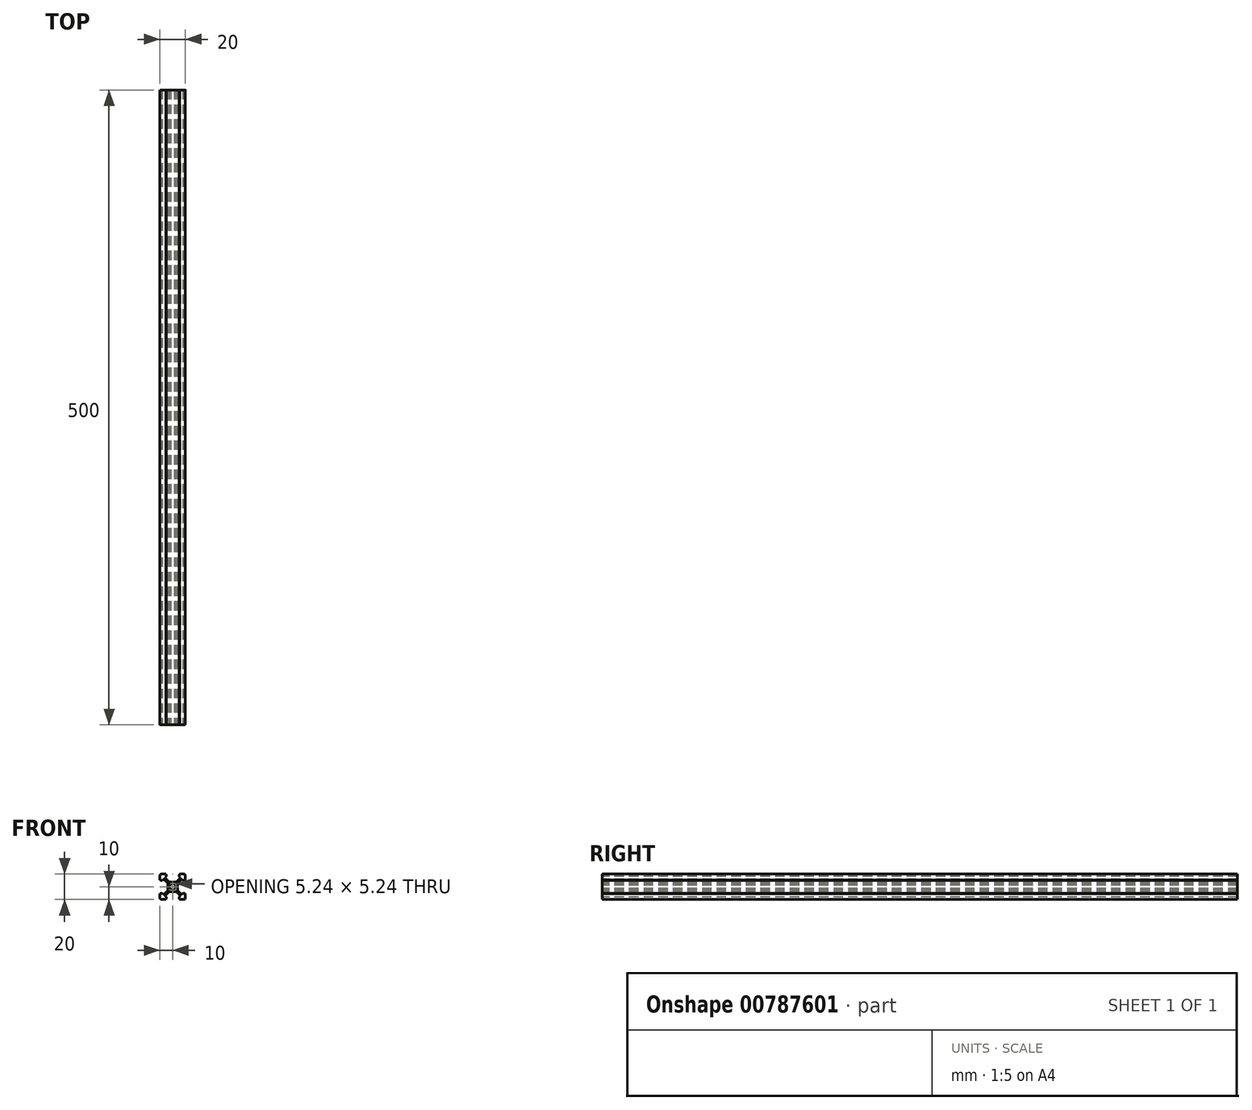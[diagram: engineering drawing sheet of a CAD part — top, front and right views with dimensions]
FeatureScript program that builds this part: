
annotation { "Feature Type Name" : "Feature", "Feature Type Description" : "" }
export const myFeature = defineFeature(function(context is Context, id is Id, definition is map)
    precondition{}
    {
        {
            var Q0;
            Q0=qCreatedBy(makeId("Front.planeOp"),FACE);
            var sketch = newSketch(context, id + "F0", { "sketchPlane" : qUnion([Q0])});
            skLineSegment(sketch, "E0", {"start": v(-10, 5.5) * mm, "end": v(-10, 9) * mm});
            skLineSegment(sketch, "E1", {"start": v(-9, 10) * mm, "end": v(-5.5, 10) * mm});
            skPoint(sketch, "E2.visualSharp", {"position": v(-10, 10) * mm});
            skArc(sketch, "E2.filletArc", {"start": v(-9, 10) * mm, "mid": v(-9.7, 9.7) * mm, "end": v(-10, 9) * mm});
            skPoint(sketch, "E3.end.orphan", {"position": v(0, 8) * mm});
            skPoint(sketch, "E4.start.orphan", {"position": v(-8, 0) * mm});
            skLineSegment(sketch, "E5", {"start": v(-10, 5.5) * mm, "end": v(-9.5, 5.5) * mm});
            skLineSegment(sketch, "E6", {"start": v(-9.5, 5.5) * mm, "end": v(-9.5, 5) * mm});
            skLineSegment(sketch, "E7", {"start": v(-9.5, 5) * mm, "end": v(-8.1, 5) * mm});
            skLineSegment(sketch, "E8", {"start": v(-8.1, 4.97) * mm, "end": v(-8.1, 5) * mm});
            skPoint(sketch, "E9.end.orphan", {"position": v(-3.5, 0) * mm});
            skLineSegment(sketch, "E10.bottom", {"start": v(2.84, 3.9) * mm, "end": v(-2.84, 3.9) * mm});
            skLineSegment(sketch, "E10.top", {"start": v(2.84, -3.9) * mm, "end": v(-2.84, -3.9) * mm});
            skLineSegment(sketch, "E10.left", {"start": v(3.9, 2.84) * mm, "end": v(3.9, -2.84) * mm});
            skLineSegment(sketch, "E10.right", {"start": v(-3.9, 2.84) * mm, "end": v(-3.9, -2.84) * mm});
            skPoint(sketch, "E10.middle", {"position": v(0, 0) * mm});
            skPoint(sketch, "E11.orphan", {"position": v(0, 9) * mm});
            skLineSegment(sketch, "E12.MirrorCS", {"start": v(-5.5, 10) * mm, "end": v(-9, 10) * mm});
            skLineSegment(sketch, "E13.MirrorCS", {"start": v(-5.5, 10) * mm, "end": v(-5.5, 9.5) * mm});
            skLineSegment(sketch, "E14.MirrorCS", {"start": v(-5.5, 9.5) * mm, "end": v(-5, 9.5) * mm});
            skLineSegment(sketch, "E15.MirrorCS", {"start": v(-5, 9.5) * mm, "end": v(-5, 8.1) * mm});
            skArc(sketch, "E16", {"start": v(-2.09, 1.38) * mm, "mid": v(-2.5, 0) * mm, "end": v(-2.09, -1.38) * mm});
            skLineSegment(sketch, "E17", {"start": v(-8.1, 5) * mm, "end": v(-7.33, 5.77) * mm});
            skLineSegment(sketch, "E18", {"start": v(-5.77, 6.62) * mm, "end": v(-3.2, 4.05) * mm});
            skLineSegment(sketch, "E19", {"start": v(-4.05, 3.2) * mm, "end": v(-6.62, 5.77) * mm});
            skLineSegment(sketch, "E20", {"start": v(-1.38, 2.09) * mm, "end": v(-1.77, 2.47) * mm});
            skLineSegment(sketch, "E21.trimOffspring", {"start": v(-5.77, 7.33) * mm, "end": v(-5, 8.1) * mm});
            skPoint(sketch, "E22.end.orphan", {"position": v(-6.55, 6.55) * mm});
            skLineSegment(sketch, "E23", {"start": v(-2.09, 1.38) * mm, "end": v(-2.47, 1.77) * mm});
            skLineSegment(sketch, "E24", {"start": v(-2.47, 2.47) * mm, "end": v(-2.47, 2.47) * mm});
            skArc(sketch, "E25.filletArc", {"start": v(-1.77, 2.47) * mm, "mid": v(-2.12, 2.62) * mm, "end": v(-2.47, 2.47) * mm});
            skArc(sketch, "E26.filletArc", {"start": v(-2.47, 2.47) * mm, "mid": v(-2.62, 2.12) * mm, "end": v(-2.47, 1.77) * mm});
            skArc(sketch, "E27.filletArc", {"start": v(-5.77, 7.33) * mm, "mid": v(-5.92, 6.97) * mm, "end": v(-5.77, 6.62) * mm});
            skPoint(sketch, "E28.visualSharp", {"position": v(-6.97, 6.13) * mm});
            skArc(sketch, "E28.filletArc", {"start": v(-6.62, 5.77) * mm, "mid": v(-6.97, 5.92) * mm, "end": v(-7.33, 5.77) * mm});
            skPoint(sketch, "E29.newPointB", {"position": v(-3.9, 3.9) * mm});
            skArc(sketch, "E29.filletArc", {"start": v(-3.2, 4.05) * mm, "mid": v(-3.04, 3.94) * mm, "end": v(-2.84, 3.9) * mm});
            skArc(sketch, "E30.filletArc", {"start": v(-3.9, 2.84) * mm, "mid": v(-3.94, 3.04) * mm, "end": v(-4.05, 3.2) * mm});
            skPoint(sketch, "E31.end.orphan", {"position": v(-0.76, 0.76) * mm});
            skPoint(sketch, "E31.start.orphan", {"position": v(-1.18, 0.33) * mm});
            skPoint(sketch, "E32.trimOffspring.end.orphan", {"position": v(-0.33, 1.18) * mm});
            skArc(sketch, "E33.MirrorCS", {"start": v(1.38, -2.09) * mm, "mid": v(0, -2.5) * mm, "end": v(-1.38, -2.09) * mm});
            skLineSegment(sketch, "E34.MirrorCS", {"start": v(1.38, -2.09) * mm, "end": v(1.77, -2.47) * mm});
            skArc(sketch, "E35.MirrorCS", {"start": v(2.47, -2.47) * mm, "mid": v(2.12, -2.62) * mm, "end": v(1.77, -2.47) * mm});
            skArc(sketch, "E36.MirrorCS", {"start": v(2.47, -1.77) * mm, "mid": v(2.62, -2.12) * mm, "end": v(2.47, -2.47) * mm});
            skLineSegment(sketch, "E37.MirrorCS", {"start": v(2.09, -1.38) * mm, "end": v(2.47, -1.77) * mm});
            skArc(sketch, "E38.MirrorCS", {"start": v(2.84, -3.9) * mm, "mid": v(3.04, -3.94) * mm, "end": v(3.2, -4.05) * mm});
            skArc(sketch, "E39.MirrorCS", {"start": v(4.05, -3.2) * mm, "mid": v(3.94, -3.04) * mm, "end": v(3.9, -2.84) * mm});
            skLineSegment(sketch, "E40.MirrorCS", {"start": v(3.2, -4.05) * mm, "end": v(5.77, -6.62) * mm});
            skLineSegment(sketch, "E41.MirrorCS", {"start": v(6.62, -5.77) * mm, "end": v(4.05, -3.2) * mm});
            skArc(sketch, "E42.MirrorCS", {"start": v(5.77, -6.62) * mm, "mid": v(5.92, -6.97) * mm, "end": v(5.77, -7.33) * mm});
            skArc(sketch, "E43.MirrorCS", {"start": v(7.33, -5.77) * mm, "mid": v(6.97, -5.92) * mm, "end": v(6.62, -5.77) * mm});
            skLineSegment(sketch, "E44.MirrorCS", {"start": v(5, -8.1) * mm, "end": v(5.77, -7.33) * mm});
            skLineSegment(sketch, "E45.MirrorCS", {"start": v(5, -9.5) * mm, "end": v(5, -8.1) * mm});
            skLineSegment(sketch, "E46.MirrorCS", {"start": v(5.5, -10) * mm, "end": v(9, -10) * mm});
            skArc(sketch, "E47.MirrorCS", {"start": v(10, -9) * mm, "mid": v(9.7, -9.7) * mm, "end": v(9, -10) * mm});
            skLineSegment(sketch, "E48.MirrorCS", {"start": v(10, -5.5) * mm, "end": v(10, -9) * mm});
            skLineSegment(sketch, "E49.MirrorCS", {"start": v(9.5, -5) * mm, "end": v(8.1, -5) * mm});
            skLineSegment(sketch, "E50.MirrorCS", {"start": v(7.33, -5.77) * mm, "end": v(8.1, -5) * mm});
            skLineSegment(sketch, "E51.MirrorCS", {"start": v(9.5, -5.5) * mm, "end": v(9.5, -5) * mm});
            skLineSegment(sketch, "E52.MirrorCS", {"start": v(5.5, -10) * mm, "end": v(5.5, -9.5) * mm});
            skLineSegment(sketch, "E53.MirrorCS", {"start": v(5.5, -9.5) * mm, "end": v(5, -9.5) * mm});
            skLineSegment(sketch, "E54.MirrorCS", {"start": v(10, -5.5) * mm, "end": v(9.5, -5.5) * mm});
            skArc(sketch, "E55.trimOffspring", {"start": v(2.09, -1.38) * mm, "mid": v(2.5, 0) * mm, "end": v(2.09, 1.38) * mm});
            skPoint(sketch, "E56.orphan", {"position": v(3.9, -3.9) * mm});
            skLineSegment(sketch, "E57.MirrorCS", {"start": v(10, 5.5) * mm, "end": v(10, 9) * mm});
            skArc(sketch, "E58.MirrorCS", {"start": v(9, 10) * mm, "mid": v(9.7, 9.7) * mm, "end": v(10, 9) * mm});
            skLineSegment(sketch, "E59.MirrorCS", {"start": v(5.5, 10) * mm, "end": v(9, 10) * mm});
            skLineSegment(sketch, "E60.MirrorCS", {"start": v(5, 9.5) * mm, "end": v(5, 8.1) * mm});
            skLineSegment(sketch, "E61.MirrorCS", {"start": v(5.77, 7.33) * mm, "end": v(5, 8.1) * mm});
            skLineSegment(sketch, "E62.MirrorCS", {"start": v(8.1, 5) * mm, "end": v(7.33, 5.77) * mm});
            skLineSegment(sketch, "E63.MirrorCS", {"start": v(9.5, 5) * mm, "end": v(8.1, 5) * mm});
            skLineSegment(sketch, "E64.MirrorCS", {"start": v(4.05, 3.2) * mm, "end": v(6.62, 5.77) * mm});
            skLineSegment(sketch, "E65.MirrorCS", {"start": v(5.77, 6.62) * mm, "end": v(3.2, 4.05) * mm});
            skLineSegment(sketch, "E66.MirrorCS", {"start": v(-3.2, -4.05) * mm, "end": v(-5.77, -6.62) * mm});
            skLineSegment(sketch, "E67.MirrorCS", {"start": v(-6.62, -5.77) * mm, "end": v(-4.05, -3.2) * mm});
            skArc(sketch, "E68.MirrorCS", {"start": v(-7.33, -5.77) * mm, "mid": v(-6.97, -5.92) * mm, "end": v(-6.62, -5.77) * mm});
            skArc(sketch, "E69.MirrorCS", {"start": v(-5.77, -6.62) * mm, "mid": v(-5.92, -6.97) * mm, "end": v(-5.77, -7.33) * mm});
            skLineSegment(sketch, "E70.MirrorCS", {"start": v(-7.33, -5.77) * mm, "end": v(-8.1, -5) * mm});
            skLineSegment(sketch, "E71.MirrorCS", {"start": v(-9.5, -5) * mm, "end": v(-8.1, -5) * mm});
            skLineSegment(sketch, "E72.MirrorCS", {"start": v(-10, -5.5) * mm, "end": v(-10, -9) * mm});
            skArc(sketch, "E73.MirrorCS", {"start": v(-10, -9) * mm, "mid": v(-9.7, -9.7) * mm, "end": v(-9, -10) * mm});
            skLineSegment(sketch, "E74.MirrorCS", {"start": v(-5.5, -10) * mm, "end": v(-9, -10) * mm});
            skLineSegment(sketch, "E75.MirrorCS", {"start": v(-5, -9.5) * mm, "end": v(-5, -8.1) * mm});
            skLineSegment(sketch, "E76.MirrorCS", {"start": v(-5, -8.1) * mm, "end": v(-5.77, -7.33) * mm});
            skArc(sketch, "E77.MirrorCS", {"start": v(-2.47, -2.47) * mm, "mid": v(-2.12, -2.62) * mm, "end": v(-1.77, -2.47) * mm});
            skArc(sketch, "E78.MirrorCS", {"start": v(-2.47, -1.77) * mm, "mid": v(-2.62, -2.12) * mm, "end": v(-2.47, -2.47) * mm});
            skLineSegment(sketch, "E79.MirrorCS", {"start": v(-1.38, -2.09) * mm, "end": v(-1.77, -2.47) * mm});
            skLineSegment(sketch, "E80.MirrorCS", {"start": v(-2.09, -1.38) * mm, "end": v(-2.47, -1.77) * mm});
            skLineSegment(sketch, "E81.MirrorCS", {"start": v(1.38, 2.09) * mm, "end": v(1.77, 2.47) * mm});
            skArc(sketch, "E82.MirrorCS", {"start": v(1.77, 2.47) * mm, "mid": v(2.12, 2.62) * mm, "end": v(2.47, 2.47) * mm});
            skArc(sketch, "E83.MirrorCS", {"start": v(2.47, 2.47) * mm, "mid": v(2.62, 2.12) * mm, "end": v(2.47, 1.77) * mm});
            skLineSegment(sketch, "E84.MirrorCS", {"start": v(2.09, 1.38) * mm, "end": v(2.47, 1.77) * mm});
            skArc(sketch, "E85.MirrorCS", {"start": v(-2.84, -3.9) * mm, "mid": v(-3.04, -3.94) * mm, "end": v(-3.2, -4.05) * mm});
            skArc(sketch, "E86.MirrorCS", {"start": v(-4.05, -3.2) * mm, "mid": v(-3.94, -3.04) * mm, "end": v(-3.9, -2.84) * mm});
            skArc(sketch, "E87.MirrorCS", {"start": v(3.9, 2.84) * mm, "mid": v(3.94, 3.04) * mm, "end": v(4.05, 3.2) * mm});
            skArc(sketch, "E88.MirrorCS", {"start": v(3.2, 4.05) * mm, "mid": v(3.04, 3.94) * mm, "end": v(2.84, 3.9) * mm});
            skLineSegment(sketch, "E89.MirrorCS", {"start": v(-5.5, -9.5) * mm, "end": v(-5, -9.5) * mm});
            skLineSegment(sketch, "E90.MirrorCS", {"start": v(-5.5, -10) * mm, "end": v(-5.5, -9.5) * mm});
            skLineSegment(sketch, "E91.MirrorCS", {"start": v(-9.5, -5.5) * mm, "end": v(-9.5, -5) * mm});
            skLineSegment(sketch, "E92.MirrorCS", {"start": v(-10, -5.5) * mm, "end": v(-9.5, -5.5) * mm});
            skLineSegment(sketch, "E93.MirrorCS", {"start": v(5.5, 10) * mm, "end": v(5.5, 9.5) * mm});
            skLineSegment(sketch, "E94.MirrorCS", {"start": v(5.5, 9.5) * mm, "end": v(5, 9.5) * mm});
            skArc(sketch, "E95.MirrorCS", {"start": v(5.77, 7.33) * mm, "mid": v(5.92, 6.97) * mm, "end": v(5.77, 6.62) * mm});
            skArc(sketch, "E96.MirrorCS", {"start": v(6.62, 5.77) * mm, "mid": v(6.97, 5.92) * mm, "end": v(7.33, 5.77) * mm});
            skLineSegment(sketch, "E97.MirrorCS", {"start": v(9.5, 5.5) * mm, "end": v(9.5, 5) * mm});
            skLineSegment(sketch, "E98.MirrorCS", {"start": v(10, 5.5) * mm, "end": v(9.5, 5.5) * mm});
            skArc(sketch, "E99.trimOffspring", {"start": v(-1.38, 2.09) * mm, "mid": v(0, 2.5) * mm, "end": v(1.38, 2.09) * mm});
            skArc(sketch, "E100.trimOffspring", {"start": v(-1.38, -2.09) * mm, "mid": v(0, -2.5) * mm, "end": v(1.38, -2.09) * mm});
            skArc(sketch, "E101.trimOffspring", {"start": v(1.38, 2.09) * mm, "mid": v(0, 2.5) * mm, "end": v(-1.38, 2.09) * mm});
            skArc(sketch, "E102.trimOffspring", {"start": v(2.09, 1.38) * mm, "mid": v(2.5, 0) * mm, "end": v(2.09, -1.38) * mm});
            skArc(sketch, "E103.trimOffspring", {"start": v(-2.09, -1.38) * mm, "mid": v(-2.5, 0) * mm, "end": v(-2.09, 1.38) * mm});
            skPoint(sketch, "E104.orphan", {"position": v(-3.9, -3.9) * mm});
            skPoint(sketch, "E105.orphan", {"position": v(3.9, 3.9) * mm});
            skSolve(sketch);
        }
        {
            var Q0;
            Q0 = qSketchRegion(id + "F0", true);
            extrude(context, id + "F1", {"entities" : qUnion([Q0]), "oppositeDirection" : true, "depth" : 500 * mm, "offsetDistance" : 25 * mm});
        }
    });
